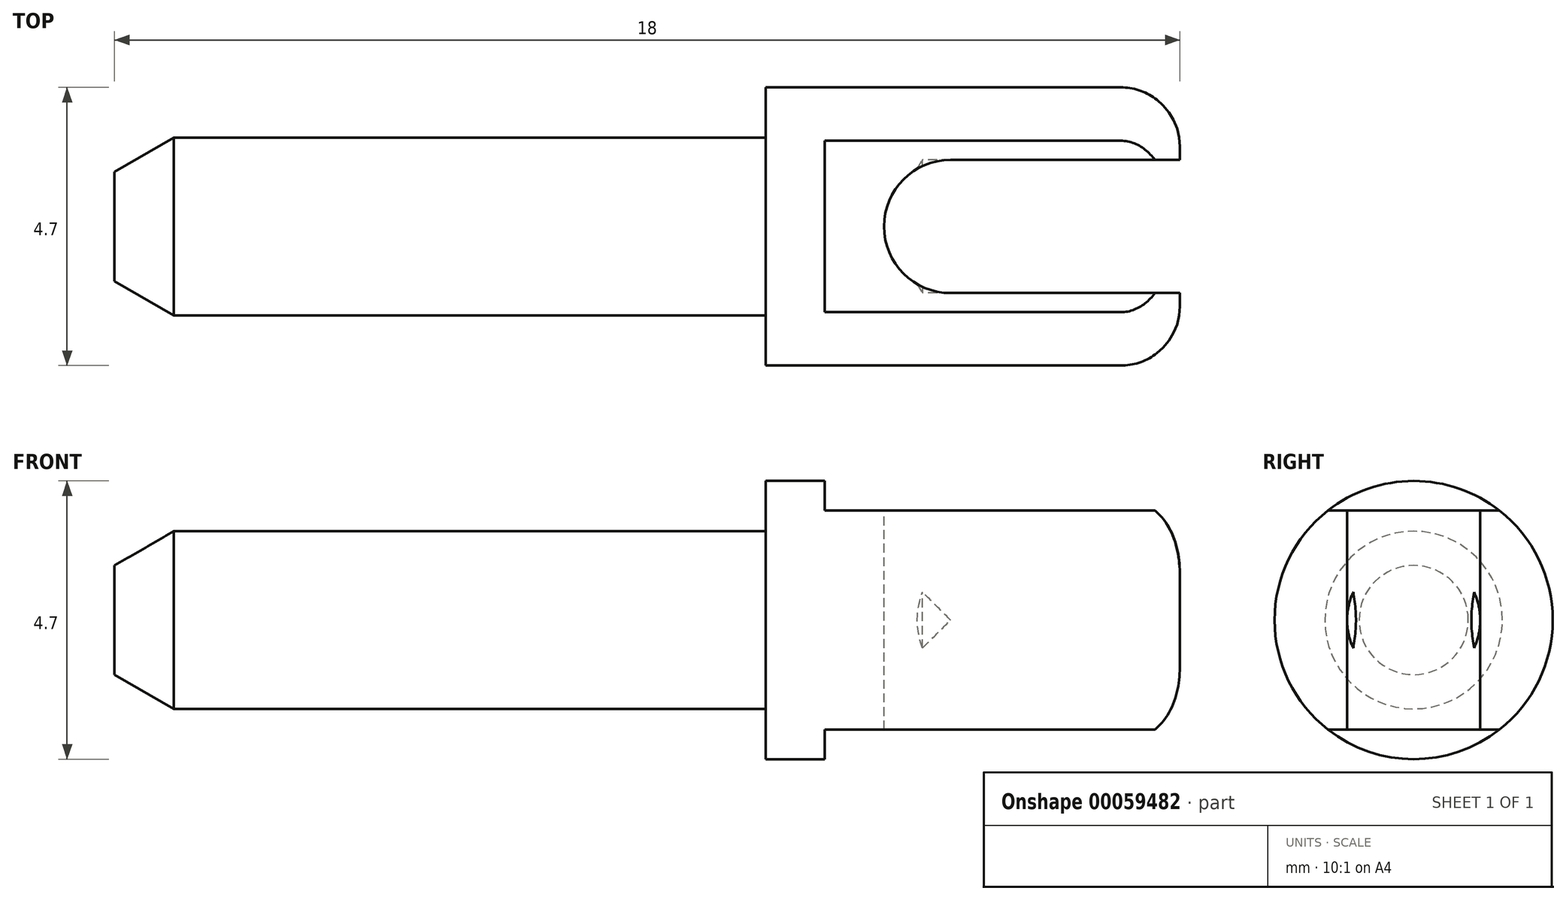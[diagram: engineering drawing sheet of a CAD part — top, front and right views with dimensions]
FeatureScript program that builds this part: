
annotation { "Feature Type Name" : "Feature", "Feature Type Description" : "" }
export const myFeature = defineFeature(function(context is Context, id is Id, definition is map)
    precondition{}
    {
        {
            var Q0;
            Q0=qCreatedBy(makeId("Front.planeOp"),FACE);
            var sketch = newSketch(context, id + "F0", { "sketchPlane" : qUnion([Q0])});
            skLineSegment(sketch, "E0", {"start": v(0, 0) * mm, "end": v(0.65, 1.12) * mm});
            skLineSegment(sketch, "E1", {"start": v(0.65, 1.13) * mm, "end": v(5, 1.13) * mm});
            skLineSegment(sketch, "E2", {"start": v(5, 1.13) * mm, "end": v(5, 2.35) * mm});
            skLineSegment(sketch, "E3", {"start": v(5, 2.35) * mm, "end": v(-2, 2.35) * mm});
            skLineSegment(sketch, "E4", {"start": v(-2, 2.35) * mm, "end": v(-2, 1.5) * mm});
            skLineSegment(sketch, "E5", {"start": v(-2, 1.5) * mm, "end": v(-12, 1.5) * mm});
            skLineSegment(sketch, "E6", {"start": v(-12, 1.5) * mm, "end": v(-13, 0.92) * mm});
            skLineSegment(sketch, "E7", {"start": v(-13, 0.92) * mm, "end": v(-13, 0) * mm});
            skLineSegment(sketch, "E8", {"start": v(-13, 0) * mm, "end": v(0, 0) * mm});
            skLineSegment(sketch, "E9", {"start": v(0, 0) * mm, "end": v(9.18, 0) * mm, "construction": true});
            skSolve(sketch);
        }
        {
            var Q0;
            Q0 = qSketchRegion(id + "F0", true);
            var Q1;
            Q1=sQuery(id+"F0.wireOp",EDGE,"E9");
            revolve(context, id + "F1", {"entities" : qUnion([Q0]), "axis" : qUnion([Q1]), "revolveType" : RevolveType.FULL});
        }
        {
            var Q0;
            Q0=makeQuery(id+"F1.opRevolve","SWEPT_FACE",FACE,{"disambiguationData":[OSD([sQuery(id+"F0.wireOp",EDGE,"E2")])]});
            var sketch = newSketch(context, id + "F2", { "sketchPlane" : qUnion([Q0])});
            skLineSegment(sketch, "E10", {"start": v(-1.45, 1.85) * mm, "end": v(1.45, 1.85) * mm});
            skArc(sketch, "E11.0", {"start": v(1.45, 1.85) * mm, "mid": v(0, 2.35) * mm, "end": v(-1.45, 1.85) * mm});
            skLineSegment(sketch, "E12", {"start": v(0, 0) * mm, "end": v(11.28, 0) * mm, "construction": true});
            skLineSegment(sketch, "E13.MirrorCS", {"start": v(-1.45, -1.85) * mm, "end": v(1.45, -1.85) * mm});
            skArc(sketch, "E14.MirrorCS", {"start": v(1.45, -1.85) * mm, "mid": v(0, -2.35) * mm, "end": v(-1.45, -1.85) * mm});
            skSolve(sketch);
        }
        {
            var Q0;
            Q0 = qSketchRegion(id + "F2", true);
            extrude(context, id + "F3", {"entities" : qUnion([Q0]), "operationType" : NewBodyOperationType.REMOVE, "oppositeDirection" : true, "depth" : 6 * mm});
        }
        {
            var Q0;
            Q0=makeQuery(id+"F3.boolean.opBoolean","COPY",FACE,{"derivedFrom":makeQuery(id+"F3.opExtrude","SWEPT_FACE",FACE,{"disambiguationData":[OSD([sQuery(id+"F2.wireOp",EDGE,"E10")])]})});
            var sketch = newSketch(context, id + "F4", { "sketchPlane" : qUnion([Q0])});
            skArc(sketch, "E15", {"start": v(1.12, 1.13) * mm, "mid": v(0, 0) * mm, "end": v(1.12, -1.13) * mm});
            skLineSegment(sketch, "E16", {"start": v(1.13, 0) * mm, "end": v(1.13, 1.13) * mm, "construction": true});
            skLineSegment(sketch, "E17", {"start": v(1.13, 0) * mm, "end": v(1.13, -1.13) * mm, "construction": true});
            skLineSegment(sketch, "E18", {"start": v(1.13, 1.13) * mm, "end": v(7.15, 1.13) * mm});
            skLineSegment(sketch, "E19", {"start": v(7.15, 1.13) * mm, "end": v(7.15, -1.13) * mm});
            skLineSegment(sketch, "E20", {"start": v(7.15, -1.13) * mm, "end": v(1.13, -1.13) * mm});
            skSolve(sketch);
        }
        {
            var Q0;
            Q0 = qSketchRegion(id + "F4", true);
            extrude(context, id + "F5", {"entities" : qUnion([Q0]), "operationType" : NewBodyOperationType.REMOVE, "oppositeDirection" : true, "depth" : 25 * mm});
        }
        {
            var Q0;
            Q0=makeQuery(id+"F3.boolean.opBoolean","SPLIT",EDGE,{"disambiguationData":[OD(0.0)],"derivedFrom":makeQuery(id+"F1.opRevolve","SWEPT_EDGE",EDGE,{"disambiguationData":[OSD([sQuery(id+"F0.wireOp",EDGE,"E2"),sQuery(id+"F0.wireOp",EDGE,"E3")])]})});
            var Q1;
            Q1=makeQuery(id+"F3.boolean.opBoolean","SPLIT",EDGE,{"disambiguationData":[OD(1.0)],"derivedFrom":makeQuery(id+"F1.opRevolve","SWEPT_EDGE",EDGE,{"disambiguationData":[OSD([sQuery(id+"F0.wireOp",EDGE,"E2"),sQuery(id+"F0.wireOp",EDGE,"E3")])]})});
            fillet(context, id + "F6", {"entities" : qUnion([Q0, Q1]), "radius" : 1 * mm, "tangentPropagation" : true, "allowEdgeOverflow" : false});
        }
    });
